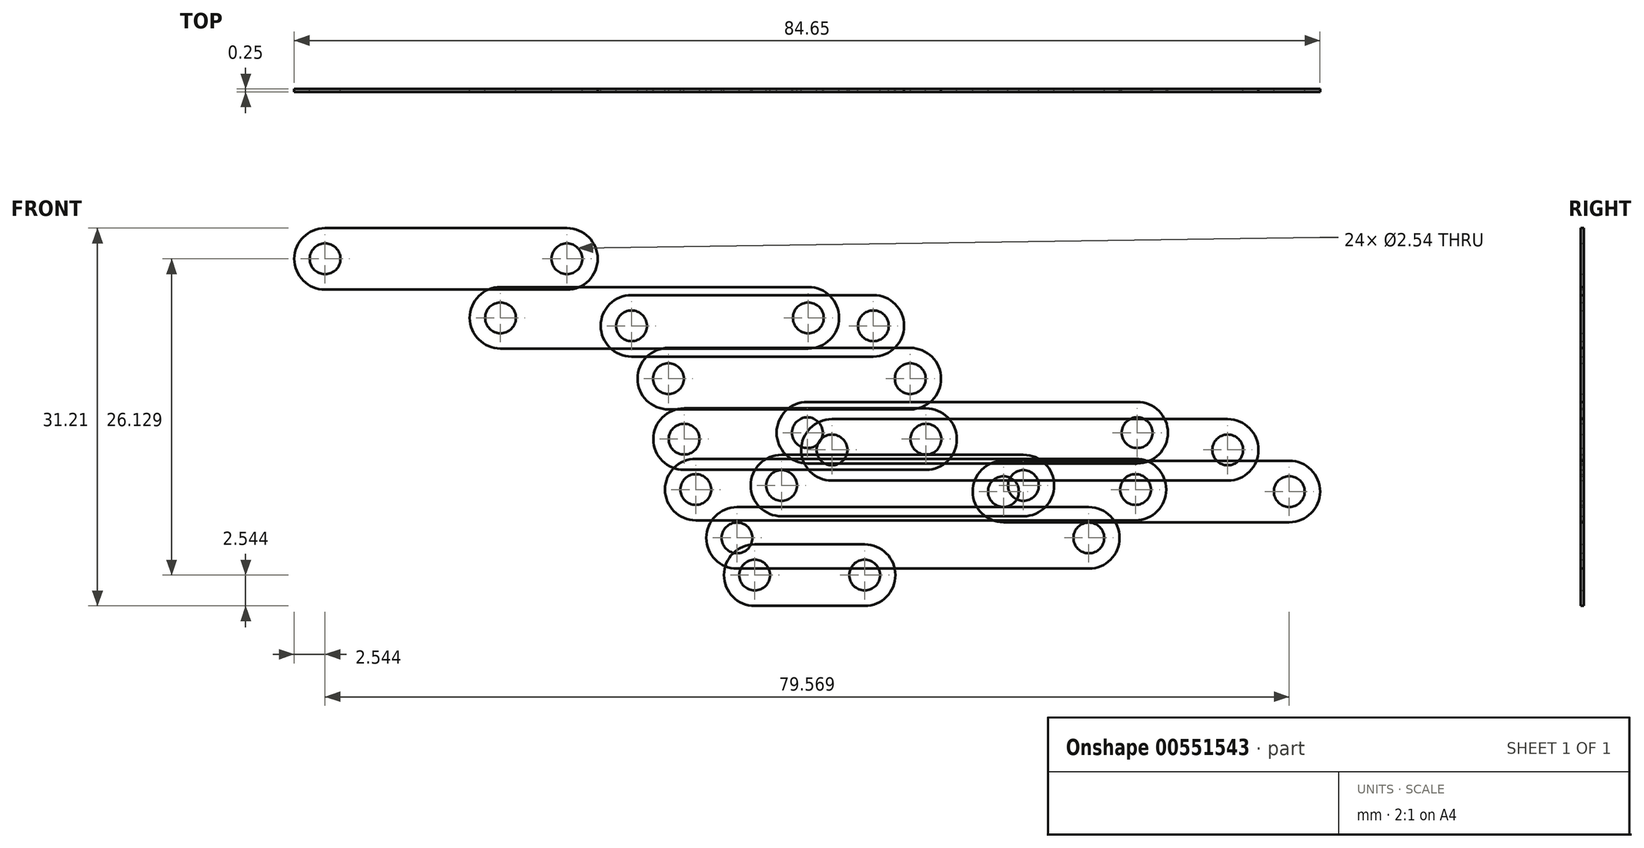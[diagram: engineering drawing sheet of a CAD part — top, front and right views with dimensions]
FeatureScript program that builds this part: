
annotation { "Feature Type Name" : "Feature", "Feature Type Description" : "" }
export const myFeature = defineFeature(function(context is Context, id is Id, definition is map)
    precondition{}
    {
        {
            assignVariable(context, id + "F0", {"name" : "thickness", "anyValue" : 0.25});
        }
        {
            var Q0;
            Q0=qCreatedBy(makeId("Front.planeOp"),FACE);
            var sketch = newSketch(context, id + "F1", { "sketchPlane" : qUnion([Q0])});
            skCircle(sketch, "E0", {"center": v(-20.38, 0) * mm, "radius": 1.27 * mm});
            skCircle(sketch, "E1", {"center": v(3.2, 0) * mm, "radius": 1.27 * mm});
            skCircle(sketch, "E2", {"center": v(-20.38, 0) * mm, "radius": 2.54 * mm});
            skCircle(sketch, "E3", {"center": v(3.2, 0) * mm, "radius": 2.54 * mm});
            skLineSegment(sketch, "E4.bottom", {"start": v(-20.38, 2.54) * mm, "end": v(3.2, 2.54) * mm});
            skLineSegment(sketch, "E4.top", {"start": v(-20.38, -2.54) * mm, "end": v(3.2, -2.54) * mm});
            skLineSegment(sketch, "E4.left", {"start": v(-20.38, 2.54) * mm, "end": v(-20.38, -2.54) * mm});
            skLineSegment(sketch, "E4.right", {"start": v(3.2, 2.54) * mm, "end": v(3.2, -2.54) * mm});
            skSolve(sketch);
        }
        {
            var Q0;
            Q0 = qSketchRegion(id + "F1", true);
            extrude(context, id + "F2", {"entities" : qUnion([Q0]), "depth" : (getVariable(context, 'thickness')) * mm, "offsetDistance" : 25.4 * mm});
        }
        {
            var Q0;
            Q0=qCreatedBy(makeId("Front.planeOp"),FACE);
            var sketch = newSketch(context, id + "F3", { "sketchPlane" : qUnion([Q0])});
            skCircle(sketch, "E5", {"center": v(-40.9, -6.9) * mm, "radius": 1.27 * mm});
            skCircle(sketch, "E6", {"center": v(-31.84, -6.9) * mm, "radius": 1.27 * mm});
            skCircle(sketch, "E7", {"center": v(-40.9, -6.9) * mm, "radius": 2.54 * mm});
            skCircle(sketch, "E8", {"center": v(-31.84, -6.9) * mm, "radius": 2.54 * mm});
            skLineSegment(sketch, "E9.bottom", {"start": v(-40.9, -4.37) * mm, "end": v(-31.84, -4.37) * mm});
            skLineSegment(sketch, "E9.top", {"start": v(-40.9, -9.45) * mm, "end": v(-31.84, -9.45) * mm});
            skLineSegment(sketch, "E9.left", {"start": v(-40.9, -4.37) * mm, "end": v(-40.9, -9.45) * mm});
            skLineSegment(sketch, "E9.right", {"start": v(-31.84, -4.37) * mm, "end": v(-31.84, -9.45) * mm});
            skSolve(sketch);
        }
        {
            var Q0;
            Q0 = qSketchRegion(id + "F3", true);
            extrude(context, id + "F4", {"entities" : qUnion([Q0]), "depth" : (getVariable(context, 'thickness')) * mm, "offsetDistance" : 25.4 * mm});
        }
        {
            var Q0;
            Q0=qCreatedBy(makeId("Front.planeOp"),FACE);
            var sketch = newSketch(context, id + "F5", { "sketchPlane" : qUnion([Q0])});
            skCircle(sketch, "E10", {"center": v(-42.37, -3.83) * mm, "radius": 1.27 * mm});
            skCircle(sketch, "E11", {"center": v(-13.34, -3.83) * mm, "radius": 1.27 * mm});
            skCircle(sketch, "E12", {"center": v(-42.37, -3.83) * mm, "radius": 2.54 * mm});
            skCircle(sketch, "E13", {"center": v(-13.34, -3.83) * mm, "radius": 2.54 * mm});
            skLineSegment(sketch, "E14.bottom", {"start": v(-42.37, -1.3) * mm, "end": v(-13.34, -1.3) * mm});
            skLineSegment(sketch, "E14.top", {"start": v(-42.37, -6.37) * mm, "end": v(-13.34, -6.37) * mm});
            skLineSegment(sketch, "E14.left", {"start": v(-42.37, -1.3) * mm, "end": v(-42.37, -6.37) * mm});
            skLineSegment(sketch, "E14.right", {"start": v(-13.34, -1.3) * mm, "end": v(-13.34, -6.37) * mm});
            skSolve(sketch);
        }
        {
            var Q0;
            Q0 = qSketchRegion(id + "F5", true);
            extrude(context, id + "F6", {"entities" : qUnion([Q0]), "depth" : (getVariable(context, 'thickness')) * mm, "offsetDistance" : 25.4 * mm});
        }
        {
            var Q0;
            Q0=qCreatedBy(makeId("Front.planeOp"),FACE);
            var sketch = newSketch(context, id + "F7", { "sketchPlane" : qUnion([Q0])});
            skCircle(sketch, "E15", {"center": v(-48.03, 9.32) * mm, "radius": 1.27 * mm});
            skCircle(sketch, "E16", {"center": v(-28.08, 9.32) * mm, "radius": 1.27 * mm});
            skCircle(sketch, "E17", {"center": v(-48.03, 9.32) * mm, "radius": 2.54 * mm});
            skCircle(sketch, "E18", {"center": v(-28.08, 9.32) * mm, "radius": 2.54 * mm});
            skLineSegment(sketch, "E19.bottom", {"start": v(-48.03, 11.86) * mm, "end": v(-28.08, 11.86) * mm});
            skLineSegment(sketch, "E19.top", {"start": v(-48.03, 6.78) * mm, "end": v(-28.08, 6.78) * mm});
            skLineSegment(sketch, "E19.left", {"start": v(-48.03, 11.86) * mm, "end": v(-48.03, 6.78) * mm});
            skLineSegment(sketch, "E19.right", {"start": v(-28.08, 11.86) * mm, "end": v(-28.08, 6.78) * mm});
            skSolve(sketch);
        }
        {
            var Q0;
            Q0 = qSketchRegion(id + "F7", true);
            extrude(context, id + "F8", {"entities" : qUnion([Q0]), "depth" : (getVariable(context, 'thickness')) * mm, "offsetDistance" : 25.4 * mm});
        }
        {
            var Q0;
            Q0=qCreatedBy(makeId("Front.planeOp"),FACE);
            var sketch = newSketch(context, id + "F9", { "sketchPlane" : qUnion([Q0])});
            skCircle(sketch, "E20", {"center": v(-38.7, 0.5) * mm, "radius": 1.27 * mm});
            skCircle(sketch, "E21", {"center": v(-18.74, 0.5) * mm, "radius": 1.27 * mm});
            skCircle(sketch, "E22", {"center": v(-38.7, 0.5) * mm, "radius": 2.54 * mm});
            skCircle(sketch, "E23", {"center": v(-18.74, 0.5) * mm, "radius": 2.54 * mm});
            skLineSegment(sketch, "E24.bottom", {"start": v(-38.7, 3.04) * mm, "end": v(-18.74, 3.04) * mm});
            skLineSegment(sketch, "E24.top", {"start": v(-38.7, -2.04) * mm, "end": v(-18.74, -2.04) * mm});
            skLineSegment(sketch, "E24.left", {"start": v(-38.7, 3.04) * mm, "end": v(-38.7, -2.04) * mm});
            skLineSegment(sketch, "E24.right", {"start": v(-18.74, 3.04) * mm, "end": v(-18.74, -2.04) * mm});
            skSolve(sketch);
        }
        {
            var Q0;
            Q0 = qSketchRegion(id + "F9", true);
            extrude(context, id + "F10", {"entities" : qUnion([Q0]), "depth" : (getVariable(context, 'thickness')) * mm, "offsetDistance" : 25.4 * mm});
        }
        {
            var Q0;
            Q0=qCreatedBy(makeId("Front.planeOp"),FACE);
            var sketch = newSketch(context, id + "F11", { "sketchPlane" : qUnion([Q0])});
            skCircle(sketch, "E25", {"center": v(-36.57, 4.86) * mm, "radius": 1.27 * mm});
            skCircle(sketch, "E26", {"center": v(-9.35, 4.86) * mm, "radius": 1.27 * mm});
            skCircle(sketch, "E27", {"center": v(-36.57, 4.86) * mm, "radius": 2.54 * mm});
            skCircle(sketch, "E28", {"center": v(-9.35, 4.86) * mm, "radius": 2.54 * mm});
            skLineSegment(sketch, "E29.bottom", {"start": v(-36.57, 7.4) * mm, "end": v(-9.35, 7.4) * mm});
            skLineSegment(sketch, "E29.top", {"start": v(-36.57, 2.32) * mm, "end": v(-9.35, 2.32) * mm});
            skLineSegment(sketch, "E29.left", {"start": v(-36.57, 7.4) * mm, "end": v(-36.57, 2.32) * mm});
            skLineSegment(sketch, "E29.right", {"start": v(-9.35, 7.4) * mm, "end": v(-9.35, 2.32) * mm});
            skSolve(sketch);
        }
        {
            var Q0;
            Q0 = qSketchRegion(id + "F11", true);
            extrude(context, id + "F12", {"entities" : qUnion([Q0]), "depth" : (getVariable(context, 'thickness')) * mm, "offsetDistance" : 25.4 * mm});
        }
        {
            var Q0;
            Q0=qCreatedBy(makeId("Front.planeOp"),FACE);
            var sketch = newSketch(context, id + "F13", { "sketchPlane" : qUnion([Q0])});
            skCircle(sketch, "E30", {"center": v(-34.54, 3.44) * mm, "radius": 1.27 * mm});
            skCircle(sketch, "E31", {"center": v(-1.88, 3.44) * mm, "radius": 1.27 * mm});
            skCircle(sketch, "E32", {"center": v(-34.54, 3.44) * mm, "radius": 2.54 * mm});
            skCircle(sketch, "E33", {"center": v(-1.88, 3.44) * mm, "radius": 2.54 * mm});
            skLineSegment(sketch, "E34.bottom", {"start": v(-34.54, 5.98) * mm, "end": v(-1.88, 5.98) * mm});
            skLineSegment(sketch, "E34.top", {"start": v(-34.54, 0.9) * mm, "end": v(-1.88, 0.9) * mm});
            skLineSegment(sketch, "E34.left", {"start": v(-34.54, 5.98) * mm, "end": v(-34.54, 0.9) * mm});
            skLineSegment(sketch, "E34.right", {"start": v(-1.88, 5.98) * mm, "end": v(-1.88, 0.9) * mm});
            skSolve(sketch);
        }
        {
            var Q0;
            Q0 = qSketchRegion(id + "F13", true);
            extrude(context, id + "F14", {"entities" : qUnion([Q0]), "depth" : (getVariable(context, 'thickness')) * mm, "offsetDistance" : 25.4 * mm});
        }
        {
            var Q0;
            Q0=qCreatedBy(makeId("Front.planeOp"),FACE);
            var sketch = newSketch(context, id + "F15", { "sketchPlane" : qUnion([Q0])});
            skCircle(sketch, "E35", {"center": v(-51.08, 13.69) * mm, "radius": 1.27 * mm});
            skCircle(sketch, "E36", {"center": v(-31.12, 13.69) * mm, "radius": 1.27 * mm});
            skCircle(sketch, "E37", {"center": v(-51.08, 13.69) * mm, "radius": 2.54 * mm});
            skCircle(sketch, "E38", {"center": v(-31.12, 13.69) * mm, "radius": 2.54 * mm});
            skLineSegment(sketch, "E39.bottom", {"start": v(-51.08, 16.23) * mm, "end": v(-31.12, 16.23) * mm});
            skLineSegment(sketch, "E39.top", {"start": v(-51.08, 11.15) * mm, "end": v(-31.12, 11.15) * mm});
            skLineSegment(sketch, "E39.left", {"start": v(-51.08, 16.23) * mm, "end": v(-51.08, 11.15) * mm});
            skLineSegment(sketch, "E39.right", {"start": v(-31.12, 16.23) * mm, "end": v(-31.12, 11.15) * mm});
            skSolve(sketch);
        }
        {
            var Q0;
            Q0 = qSketchRegion(id + "F15", true);
            extrude(context, id + "F16", {"entities" : qUnion([Q0]), "depth" : (getVariable(context, 'thickness')) * mm, "offsetDistance" : 25.4 * mm});
        }
        {
            var Q0;
            Q0=qCreatedBy(makeId("Front.planeOp"),FACE);
            var sketch = newSketch(context, id + "F17", { "sketchPlane" : qUnion([Q0])});
            skCircle(sketch, "E40", {"center": v(-76.37, 19.22) * mm, "radius": 1.27 * mm});
            skCircle(sketch, "E41", {"center": v(-56.4, 19.22) * mm, "radius": 1.27 * mm});
            skCircle(sketch, "E42", {"center": v(-76.37, 19.22) * mm, "radius": 2.54 * mm});
            skCircle(sketch, "E43", {"center": v(-56.4, 19.22) * mm, "radius": 2.54 * mm});
            skLineSegment(sketch, "E44.bottom", {"start": v(-76.37, 21.76) * mm, "end": v(-56.4, 21.76) * mm});
            skLineSegment(sketch, "E44.top", {"start": v(-76.37, 16.68) * mm, "end": v(-56.4, 16.68) * mm});
            skLineSegment(sketch, "E44.left", {"start": v(-76.37, 21.76) * mm, "end": v(-76.37, 16.68) * mm});
            skLineSegment(sketch, "E44.right", {"start": v(-56.4, 21.76) * mm, "end": v(-56.4, 16.68) * mm});
            skSolve(sketch);
        }
        {
            var Q0;
            Q0 = qSketchRegion(id + "F17", true);
            extrude(context, id + "F18", {"entities" : qUnion([Q0]), "depth" : (getVariable(context, 'thickness')) * mm, "offsetDistance" : 25.4 * mm});
        }
        {
            var Q0;
            Q0=qCreatedBy(makeId("Front.planeOp"),FACE);
            var sketch = newSketch(context, id + "F19", { "sketchPlane" : qUnion([Q0])});
            skCircle(sketch, "E45", {"center": v(-46.74, 4.33) * mm, "radius": 1.27 * mm});
            skCircle(sketch, "E46", {"center": v(-26.78, 4.33) * mm, "radius": 1.27 * mm});
            skCircle(sketch, "E47", {"center": v(-46.74, 4.33) * mm, "radius": 2.54 * mm});
            skCircle(sketch, "E48", {"center": v(-26.78, 4.33) * mm, "radius": 2.54 * mm});
            skLineSegment(sketch, "E49.bottom", {"start": v(-46.74, 6.87) * mm, "end": v(-26.78, 6.87) * mm});
            skLineSegment(sketch, "E49.top", {"start": v(-46.74, 1.79) * mm, "end": v(-26.78, 1.79) * mm});
            skLineSegment(sketch, "E49.left", {"start": v(-46.74, 6.87) * mm, "end": v(-46.74, 1.79) * mm});
            skLineSegment(sketch, "E49.right", {"start": v(-26.78, 6.87) * mm, "end": v(-26.78, 1.79) * mm});
            skSolve(sketch);
        }
        {
            var Q0;
            Q0 = qSketchRegion(id + "F19", true);
            extrude(context, id + "F20", {"entities" : qUnion([Q0]), "depth" : (getVariable(context, 'thickness')) * mm, "offsetDistance" : 25.4 * mm});
        }
        {
            var Q0;
            Q0=qCreatedBy(makeId("Front.planeOp"),FACE);
            var sketch = newSketch(context, id + "F21", { "sketchPlane" : qUnion([Q0])});
            skCircle(sketch, "E50", {"center": v(-45.77, 0.16) * mm, "radius": 1.27 * mm});
            skCircle(sketch, "E51", {"center": v(-9.49, 0.16) * mm, "radius": 1.27 * mm});
            skCircle(sketch, "E52", {"center": v(-45.77, 0.16) * mm, "radius": 2.54 * mm});
            skCircle(sketch, "E53", {"center": v(-9.49, 0.16) * mm, "radius": 2.54 * mm});
            skLineSegment(sketch, "E54.bottom", {"start": v(-45.77, 2.7) * mm, "end": v(-9.49, 2.7) * mm});
            skLineSegment(sketch, "E54.top", {"start": v(-45.77, -2.38) * mm, "end": v(-9.49, -2.38) * mm});
            skLineSegment(sketch, "E54.left", {"start": v(-45.77, 2.7) * mm, "end": v(-45.77, -2.38) * mm});
            skLineSegment(sketch, "E54.right", {"start": v(-9.49, 2.7) * mm, "end": v(-9.49, -2.38) * mm});
            skSolve(sketch);
        }
        {
            var Q0;
            Q0 = qSketchRegion(id + "F21", true);
            extrude(context, id + "F22", {"entities" : qUnion([Q0]), "depth" : (getVariable(context, 'thickness')) * mm, "offsetDistance" : 25.4 * mm});
        }
        {
            var Q0;
            Q0=qCreatedBy(makeId("Front.planeOp"),FACE);
            var sketch = newSketch(context, id + "F23", { "sketchPlane" : qUnion([Q0])});
            skCircle(sketch, "E55", {"center": v(-61.89, 14.35) * mm, "radius": 1.27 * mm});
            skCircle(sketch, "E56", {"center": v(-36.49, 14.35) * mm, "radius": 1.27 * mm});
            skCircle(sketch, "E57", {"center": v(-61.89, 14.35) * mm, "radius": 2.54 * mm});
            skCircle(sketch, "E58", {"center": v(-36.49, 14.35) * mm, "radius": 2.54 * mm});
            skLineSegment(sketch, "E59.bottom", {"start": v(-61.89, 16.9) * mm, "end": v(-36.49, 16.9) * mm});
            skLineSegment(sketch, "E59.top", {"start": v(-61.89, 11.81) * mm, "end": v(-36.49, 11.81) * mm});
            skLineSegment(sketch, "E59.left", {"start": v(-61.89, 16.9) * mm, "end": v(-61.89, 11.81) * mm});
            skLineSegment(sketch, "E59.right", {"start": v(-36.49, 16.9) * mm, "end": v(-36.49, 11.81) * mm});
            skSolve(sketch);
        }
        {
            var Q0;
            Q0 = qSketchRegion(id + "F23", true);
            extrude(context, id + "F24", {"entities" : qUnion([Q0]), "depth" : (getVariable(context, 'thickness')) * mm, "offsetDistance" : 25.4 * mm});
        }
    });
